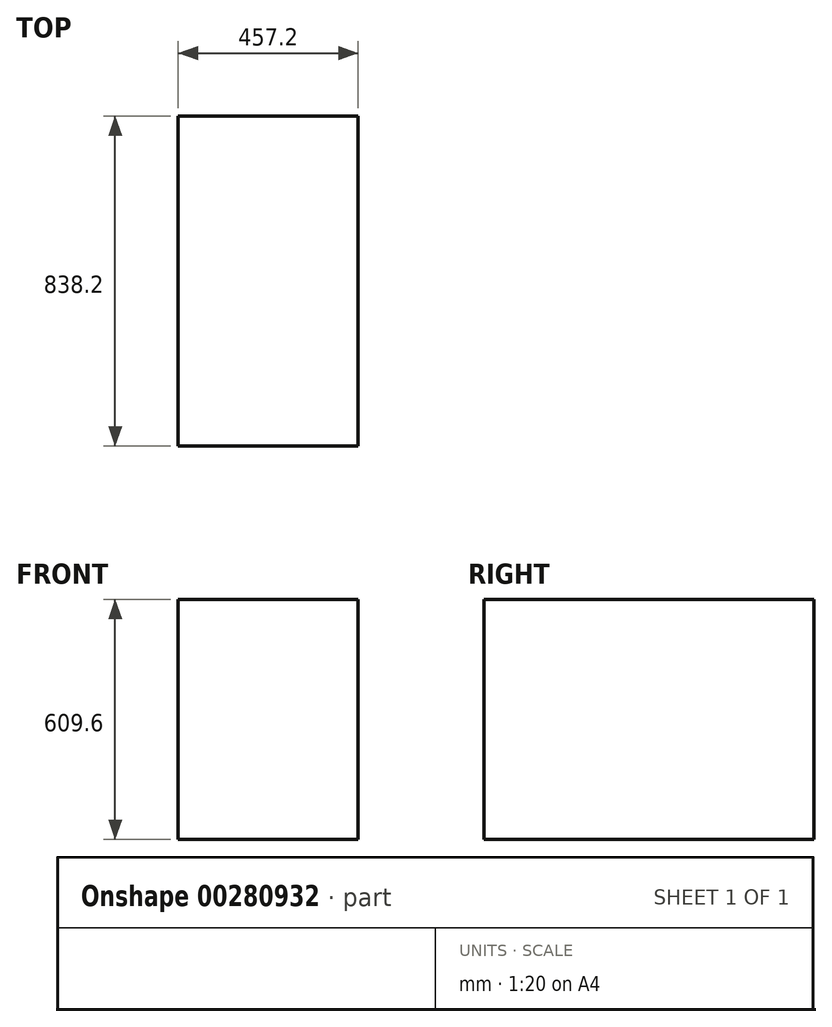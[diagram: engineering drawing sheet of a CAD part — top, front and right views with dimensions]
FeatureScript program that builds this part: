
annotation { "Feature Type Name" : "Feature", "Feature Type Description" : "" }
export const myFeature = defineFeature(function(context is Context, id is Id, definition is map)
    precondition{}
    {
        {
            var Q0;
            Q0=qCreatedBy(makeId("Top.planeOp"),FACE);
            var sketch = newSketch(context, id + "F0", { "sketchPlane" : qUnion([Q0])});
            skLineSegment(sketch, "E0.bottom", {"start": v(0, 0) * mm, "end": v(457.2, 0) * mm});
            skLineSegment(sketch, "E0.top", {"start": v(0, 838.2) * mm, "end": v(457.2, 838.2) * mm});
            skLineSegment(sketch, "E0.left", {"start": v(0, 0) * mm, "end": v(0, 838.2) * mm});
            skLineSegment(sketch, "E0.right", {"start": v(457.2, 0) * mm, "end": v(457.2, 838.2) * mm});
            skSolve(sketch);
        }
        {
            var Q0;
            Q0=makeQuery(id+"F0.imprint","IMPRINT",FACE,{"disambiguationData":[TD([[makeQuery(id+"F0.imprint","IMPRINT",EDGE,{"derivedFrom":sQuery(id+"F0.wireOp",EDGE,"E0.bottom")}),1.0]])]});
            extrude(context, id + "F1", {"entities" : qUnion([Q0]), "depth" : 609.6 * mm});
        }
    });
